# Revit family: Domotics-DomesticRanges-GEWISS-CHORUS_COMMAND-ONE-WAY_SWITCH_05M
name_source: partatom
category: Apparecchi elettrici
revit_build: Autodesk Revit 2016 (Build: 20161004_0715(x64)
units: mm (PartAtom-declared; Revit-internal decimal feet)

## family parameters
Condiviso = Sì
Host = Superficie
Mantenere orientamento annotazione = Sì
Numero OmniClass = 23.80.50.11.14
Punto di calcolo locali = Sì
Quota connettore circolare = Usa diametro
Taglio con vuoti quando caricato = Sì
Tipo di parte = Normale
Titolo OmniClass = Switches

## types (6) — shared parameters
Bidimensionale = bidimensionale interruttori 05m : GW12022
Breaking capacity: = 1.25 In (200 position changes)
Carico apparente = 0 VA
Catalogue = DOMOTICS
Catalogue Range = CHORUS - DOMESTIC RANGE
Category = One-way switch
Electrocod = 0130
Glow Wire Test = 850°C
IDF = dff03d0d-2be5-46d5-9b56-2114d3d14214
IDT = 6ffd061f-3751-4e0e-883d-b8c6425e8a49
Immagine tipo = GW14022.jpg
Insulation resistance = > 5 MOhm
Larghezza pulsante = 12 mm  [stored 0.0393701 ft]
N. poli = 1
No. Chorus modules = 1/2
Number of poles = 1P
Produttore = GEWISS S.p.A.
Prolonged operation (no.of position changes) = 40.000 at In 250 V ac cosÃ˜=0,6
Prospetto di default = 1219 mm
Resistance at test voltage = 2000 V at 50 Hz for 1 minute
SEO = 1 way switch
Simbolo = SIMBOLO INTERRUTTORI : INT1PLUM
Standard; = EN 60669-1
Technical sheet = https://www.gewiss.com
Terminal grip on cable traction = > 50 N
Terminal tightening capacity flexible cables (mm2) = min. 0,75 - max. 2x4
Terminal tightening capacity rigid cables (mm2) = min. 0,5 - max. 2x2,5
Thermo-pressure with ball = 125
Tipo_ = CHORUS INTERRUTTORI 05M_BASE : GW14022 - Titanio - Illuminabile localizzazione
URL = https://www.gewiss.com
Version file RFA = 19.0
Volt = 230 V
Voltage = 250 V ac
Voltage: = 250 V ac
Wiring terminals = With screw

## per-type parameters (varying)
| type | Button key | Colour | Description: | Descrizione | EAN code | Modello | Type |
| GW12021 - 1P - Black | Neutral | Black | 1P - 10AX | 1-WAY SWITCH, 1/2M 1P 10AX BLACK | 8011564265301 | GW12021 | General |
| GW10021 - 1P - White | Neutral | White | 1P - 10AX | 1-WAY SWITCH, 1/2M 1P 10AX WHITE | 8011564260993 | GW10021 | General |
| GW12022 - 1P - Black - Illuminable | With diffuser | Black | 1P - 10AX illuminable | 1-WAY SWITCH, 1/2M 1P 10AX ILL LOC BLACK | 8011564266117 | GW12022 | Backlit |
| GW14021 - 1P - Titanium | Neutral | Titanium | 1P - 10AX | 1-WAY SWITCH, 1/2M 1P 10AX TITANIUM | 8011564265387 | GW14021 | General |
| GW14022 - 1P - Titanium - Illuminable | With diffuser | Titanium | 1P - 10AX illuminable | 1-WAY SW. 1/2M 1P 10AX ILL LOC TITANIUM | 8011564265394 | GW14022 | Backlit |
| GW10022 - 1P - White - Illuminable | With diffuser | White | 1P - 10AX illuminable | 1-WAY SWITCH, 1/2M 1P 10AX ILL LOC WHITE | 8011564261006 | GW10022 | Backlit |

note: source unit labels omitted for Thermo-pressure with ball — the stored unit's dimension contradicts the parameter name (converter mislabeling)

note: [stored X ft] marks values corroborated as IEEE doubles in the binary element streams (Revit-internal decimal feet)

## geometry (parser evidence)
native form markers: Sweep x2
no freeform markers — native parametric forms only
